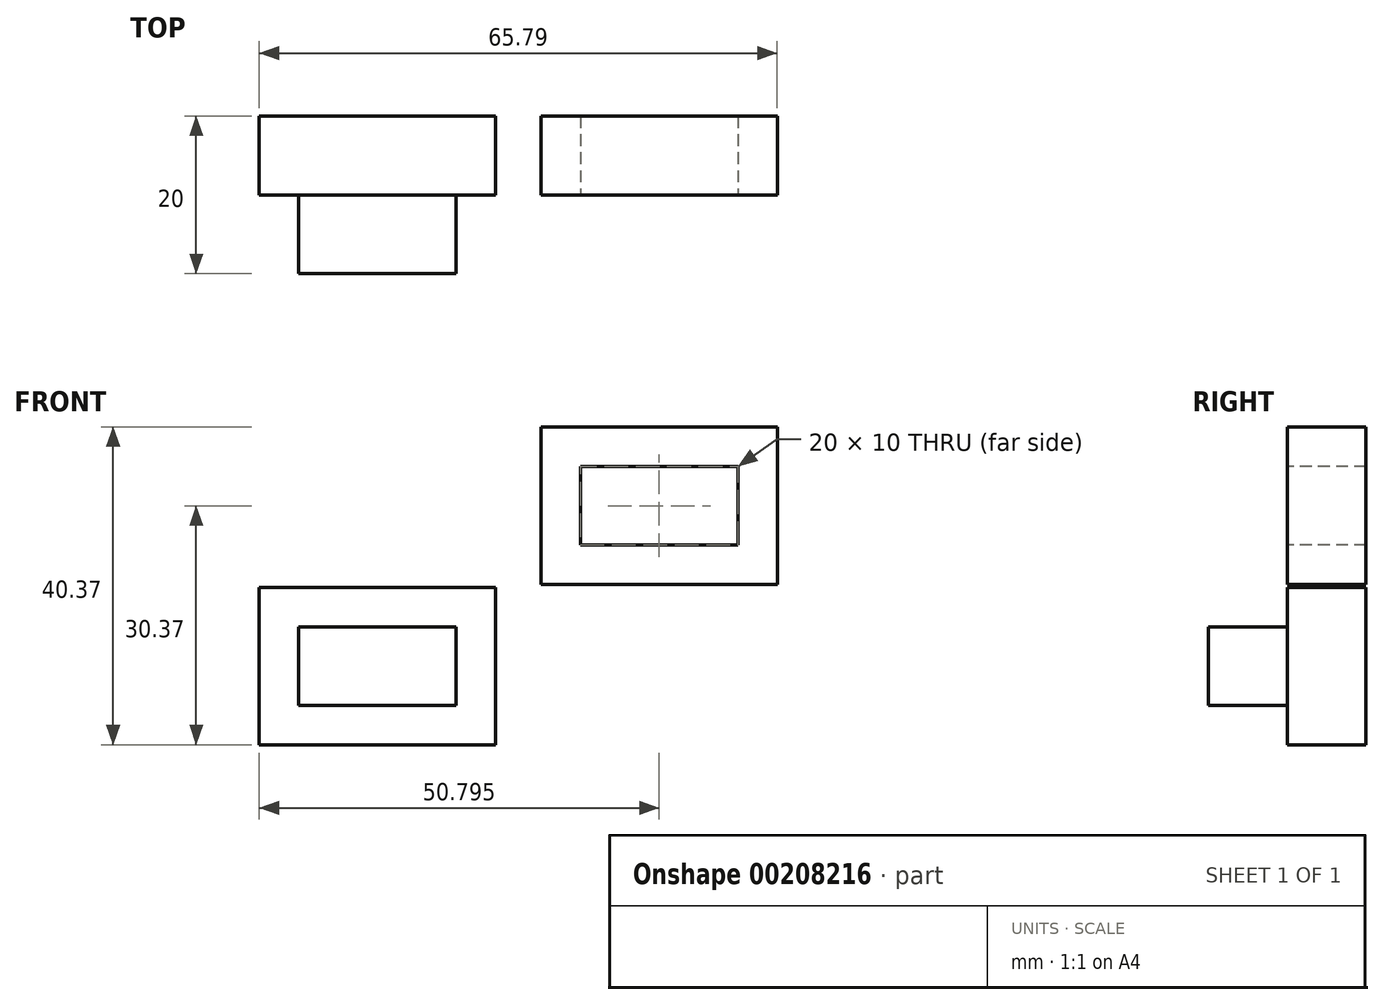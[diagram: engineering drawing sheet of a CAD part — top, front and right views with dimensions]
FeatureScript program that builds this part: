
annotation { "Feature Type Name" : "Feature", "Feature Type Description" : "" }
export const myFeature = defineFeature(function(context is Context, id is Id, definition is map)
    precondition{}
    {
        {
            var Q0;
            Q0=qCreatedBy(makeId("Front.planeOp"),FACE);
            var sketch = newSketch(context, id + "F0", { "sketchPlane" : qUnion([Q0])});
            skLineSegment(sketch, "E0.bottom", {"start": v(-20, -0.37) * mm, "end": v(10, -0.37) * mm});
            skLineSegment(sketch, "E0.top", {"start": v(-20, -20.37) * mm, "end": v(10, -20.37) * mm});
            skLineSegment(sketch, "E0.left", {"start": v(-20, -0.37) * mm, "end": v(-20, -20.37) * mm});
            skLineSegment(sketch, "E0.right", {"start": v(10, -0.37) * mm, "end": v(10, -20.37) * mm});
            skSolve(sketch);
        }
        {
            var Q0;
            Q0 = qSketchRegion(id + "F0", true);
            extrude(context, id + "F1", {"entities" : qUnion([Q0]), "depth" : 10 * mm});
        }
        {
            var Q0;
            Q0=makeQuery(id+"F1.opExtrude","CAP_FACE",FACE,{"disambiguationData":[OSD([sQuery(id+"F0.wireOp",EDGE,"E0.bottom"),sQuery(id+"F0.wireOp",EDGE,"E0.top"),sQuery(id+"F0.wireOp",EDGE,"E0.left"),sQuery(id+"F0.wireOp",EDGE,"E0.right")])],"isStart":false});
            var sketch = newSketch(context, id + "F2", { "sketchPlane" : qUnion([Q0])});
            skLineSegment(sketch, "E1.bottom", {"start": v(-15, -5.37) * mm, "end": v(5, -5.37) * mm});
            skLineSegment(sketch, "E1.top", {"start": v(-15, -15.37) * mm, "end": v(5, -15.37) * mm});
            skLineSegment(sketch, "E1.left", {"start": v(-15, -5.37) * mm, "end": v(-15, -15.37) * mm});
            skLineSegment(sketch, "E1.right", {"start": v(5, -5.37) * mm, "end": v(5, -15.37) * mm});
            skSolve(sketch);
        }
        {
            var Q0;
            Q0 = qSketchRegion(id + "F2", true);
            extrude(context, id + "F3", {"entities" : qUnion([Q0]), "operationType" : NewBodyOperationType.ADD, "depth" : 10 * mm});
        }
        {
            var Q0;
            Q0=qCreatedBy(makeId("Front.planeOp"),FACE);
            var sketch = newSketch(context, id + "F4", { "sketchPlane" : qUnion([Q0])});
            skLineSegment(sketch, "E2.bottom", {"start": v(15.8, 0) * mm, "end": v(45.8, 0) * mm});
            skLineSegment(sketch, "E2.top", {"start": v(15.8, 20) * mm, "end": v(45.8, 20) * mm});
            skLineSegment(sketch, "E2.left", {"start": v(15.8, 0) * mm, "end": v(15.8, 20) * mm});
            skLineSegment(sketch, "E2.right", {"start": v(45.8, 0) * mm, "end": v(45.8, 20) * mm});
            skSolve(sketch);
        }
        {
            var Q0;
            Q0 = qSketchRegion(id + "F4", true);
            extrude(context, id + "F5", {"entities" : qUnion([Q0]), "depth" : 10 * mm});
        }
        {
            var Q0;
            Q0=makeQuery(id+"F5.opExtrude","CAP_FACE",FACE,{"disambiguationData":[OSD([sQuery(id+"F4.wireOp",EDGE,"E2.bottom"),sQuery(id+"F4.wireOp",EDGE,"E2.top"),sQuery(id+"F4.wireOp",EDGE,"E2.left"),sQuery(id+"F4.wireOp",EDGE,"E2.right")])],"isStart":false});
            var sketch = newSketch(context, id + "F6", { "sketchPlane" : qUnion([Q0])});
            skLineSegment(sketch, "E3.bottom", {"start": v(20.8, 15) * mm, "end": v(40.8, 15) * mm});
            skLineSegment(sketch, "E3.top", {"start": v(20.8, 5) * mm, "end": v(40.8, 5) * mm});
            skLineSegment(sketch, "E3.left", {"start": v(20.8, 15) * mm, "end": v(20.8, 5) * mm});
            skLineSegment(sketch, "E3.right", {"start": v(40.8, 15) * mm, "end": v(40.8, 5) * mm});
            skSolve(sketch);
        }
        {
            var Q0;
            Q0 = qSketchRegion(id + "F6", true);
            extrude(context, id + "F7", {"entities" : qUnion([Q0]), "operationType" : NewBodyOperationType.REMOVE, "oppositeDirection" : true, "depth" : 10 * mm});
        }
    });
